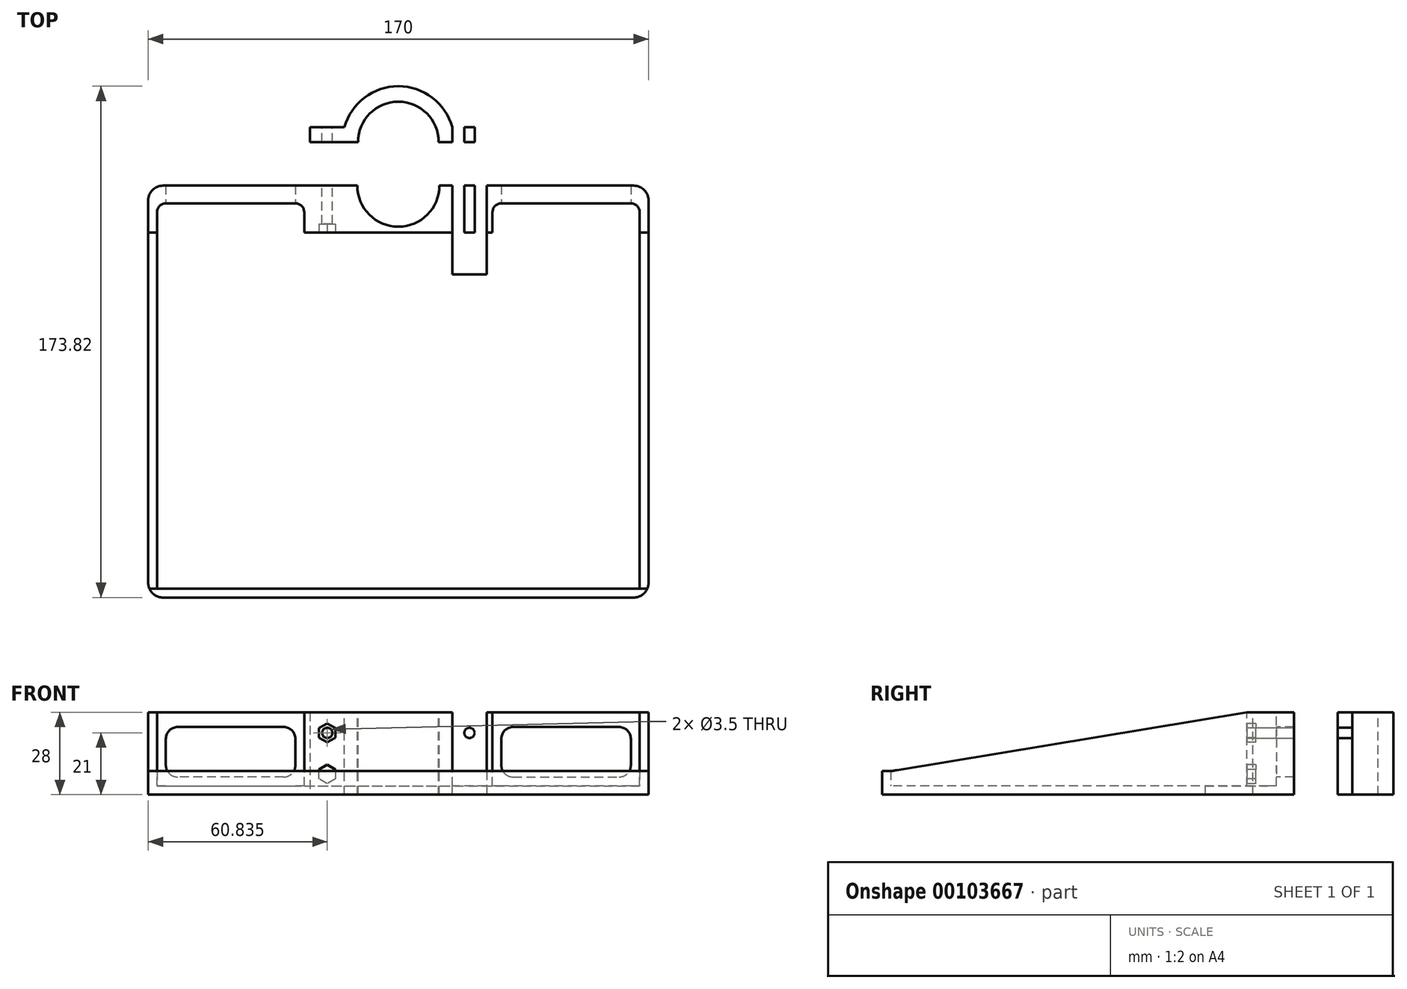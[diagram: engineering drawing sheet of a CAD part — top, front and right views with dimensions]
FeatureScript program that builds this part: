
annotation { "Feature Type Name" : "Feature", "Feature Type Description" : "" }
export const myFeature = defineFeature(function(context is Context, id is Id, definition is map)
    precondition{}
    {
        {
            var Q0;
            Q0=qCreatedBy(makeId("Top.planeOp"),FACE);
            var sketch = newSketch(context, id + "F0", { "sketchPlane" : qUnion([Q0])});
            skLineSegment(sketch, "E0.bottom", {"start": v(85, 70) * mm, "end": v(-85, 70) * mm});
            skLineSegment(sketch, "E0.top", {"start": v(85, -70) * mm, "end": v(-85, -70) * mm});
            skLineSegment(sketch, "E0.left", {"start": v(85, 70) * mm, "end": v(85, -70) * mm});
            skLineSegment(sketch, "E0.right", {"start": v(-85, 70) * mm, "end": v(-85, -70) * mm});
            skPoint(sketch, "E0.middle", {"position": v(0, 0) * mm});
            skLineSegment(sketch, "E1.bottom", {"start": v(30, 89.82) * mm, "end": v(-30, 89.82) * mm});
            skLineSegment(sketch, "E1.top", {"start": v(30, 84.82) * mm, "end": v(-30, 84.82) * mm});
            skLineSegment(sketch, "E1.left", {"start": v(30, 89.82) * mm, "end": v(30, 84.82) * mm});
            skLineSegment(sketch, "E1.right", {"start": v(-30, 89.82) * mm, "end": v(-30, 84.82) * mm});
            skPoint(sketch, "E1.middle", {"position": v(0, 87.32) * mm});
            skPoint(sketch, "E1.middle.positionSnap0", {"position": v(0, 70) * mm});
            skPoint(sketch, "E1.centerSnap0", {"position": v(0, 70) * mm});
            skSolve(sketch);
        }
        {
            var Q0;
            Q0=makeQuery(id+"F0.imprint","IMPRINT",FACE,{"disambiguationData":[TD([[makeQuery(id+"F0.imprint","IMPRINT",EDGE,{"derivedFrom":sQuery(id+"F0.wireOp",EDGE,"E0.bottom")}),1.0]])]});
            extrude(context, id + "F1", {"entities" : qUnion([Q0]), "depth" : 3 * mm});
        }
        {
            var Q0;
            Q0=makeQuery(id+"F1.opExtrude","CAP_FACE",FACE,{"disambiguationData":[OSD([sQuery(id+"F0.wireOp",EDGE,"E0.bottom"),sQuery(id+"F0.wireOp",EDGE,"E0.top"),sQuery(id+"F0.wireOp",EDGE,"E0.left"),sQuery(id+"F0.wireOp",EDGE,"E0.right")])],"isStart":false});
            var sketch = newSketch(context, id + "F2", { "sketchPlane" : qUnion([Q0])});
            skLineSegment(sketch, "E2.bottom", {"start": v(-85, 70) * mm, "end": v(85, 70) * mm});
            skLineSegment(sketch, "E2.top", {"start": v(-85, 54) * mm, "end": v(85, 54) * mm});
            skLineSegment(sketch, "E2.left", {"start": v(-85, 70) * mm, "end": v(-85, 54) * mm});
            skLineSegment(sketch, "E2.right", {"start": v(85, 70) * mm, "end": v(85, 54) * mm});
            skLineSegment(sketch, "E3.bottom", {"start": v(-85, -70) * mm, "end": v(85, -70) * mm});
            skLineSegment(sketch, "E3.top", {"start": v(-85, -67) * mm, "end": v(85, -67) * mm});
            skLineSegment(sketch, "E3.left", {"start": v(-85, -70) * mm, "end": v(-85, -67) * mm});
            skLineSegment(sketch, "E3.right", {"start": v(85, -70) * mm, "end": v(85, -67) * mm});
            skSolve(sketch);
        }
        {
            var Q0;
            Q0=makeQuery(id+"F2.imprint","IMPRINT",FACE,{"disambiguationData":[TD([[makeQuery(id+"F2.imprint","IMPRINT",EDGE,{"derivedFrom":sQuery(id+"F2.wireOp",EDGE,"E2.bottom")}),1.0]])]});
            var Q1;
            Q1=makeQuery(id+"F1.opExtrude","CAP_FACE",FACE,{"disambiguationData":[OSD([sQuery(id+"F0.wireOp",EDGE,"E1.bottom"),sQuery(id+"F0.wireOp",EDGE,"E1.top"),sQuery(id+"F0.wireOp",EDGE,"E1.left"),sQuery(id+"F0.wireOp",EDGE,"E1.right")])],"isStart":false});
            extrude(context, id + "F3", {"entities" : qUnion([Q0, Q1]), "operationType" : NewBodyOperationType.ADD, "depth" : 25 * mm});
        }
        {
            var Q0;
            Q0=makeQuery(id+"F2.imprint","IMPRINT",FACE,{"disambiguationData":[TD([[makeQuery(id+"F2.imprint","IMPRINT",EDGE,{"derivedFrom":sQuery(id+"F2.wireOp",EDGE,"E3.bottom")}),-1.0]])]});
            extrude(context, id + "F4", {"entities" : qUnion([Q0]), "operationType" : NewBodyOperationType.ADD, "depth" : 5 * mm});
        }
        {
            var Q0;
            Q0=makeQuery(id+"F3.opExtrude","CAP_FACE",FACE,{"disambiguationData":[OSD([sQuery(id+"F2.wireOp",EDGE,"E2.bottom"),sQuery(id+"F2.wireOp",EDGE,"E2.top"),sQuery(id+"F2.wireOp",EDGE,"E2.left"),sQuery(id+"F2.wireOp",EDGE,"E2.right")])],"isStart":false});
            var sketch = newSketch(context, id + "F5", { "sketchPlane" : qUnion([Q0])});
            skCircle(sketch, "E4", {"center": v(0, 70) * mm, "radius": 13.95 * mm});
            skSolve(sketch);
        }
        {
            var Q0;
            {var subQ0=sQuery(id+"F5.wireOp",EDGE,"E4");var subQ1=makeQuery(id+"F3.opExtrude","CAP_EDGE",EDGE,{"disambiguationData":[OSD([sQuery(id+"F2.wireOp",EDGE,"E2.bottom")])],"isStart":false});var subQ2=makeQuery(id+"F5.imprint","INTERSECT",VERTEX,{"disambiguationData":[OD(0.0)],"derivedFrom":[subQ1,subQ0]});Q0=makeQuery(id+"F5.imprint","IMPRINT",FACE,{"disambiguationData":[TD([[makeQuery(id+"F5.imprint","IMPRINT",EDGE,{"disambiguationData":[TD([[subQ2,-1.0]])],"derivedFrom":subQ0}),1.0]])]});}
            var Q1;
            {var subQ0=sQuery(id+"F5.wireOp",EDGE,"E4");var subQ1=makeQuery(id+"F3.opExtrude","CAP_EDGE",EDGE,{"disambiguationData":[OSD([sQuery(id+"F2.wireOp",EDGE,"E2.bottom")])],"isStart":false});var subQ2=makeQuery(id+"F5.imprint","INTERSECT",VERTEX,{"disambiguationData":[OD(0.0)],"derivedFrom":[subQ1,subQ0]});Q1=makeQuery(id+"F5.imprint","IMPRINT",FACE,{"disambiguationData":[TD([[makeQuery(id+"F5.imprint","IMPRINT",EDGE,{"disambiguationData":[TD([[subQ2,1.0]])],"derivedFrom":subQ0}),1.0]])]});}
            var Q2;
            Q2=makeQuery(id+"F1.opExtrude","CAP_FACE",FACE,{"disambiguationData":[OSD([sQuery(id+"F0.wireOp",EDGE,"E0.bottom"),sQuery(id+"F0.wireOp",EDGE,"E0.top"),sQuery(id+"F0.wireOp",EDGE,"E0.left"),sQuery(id+"F0.wireOp",EDGE,"E0.right")])],"isStart":true});
            extrude(context, id + "F6", {"entities" : qUnion([Q0, Q1]), "operationType" : NewBodyOperationType.REMOVE, "endBound" : BoundingType.UP_TO_SURFACE, "oppositeDirection" : true, "endBoundEntityFace" : qUnion([Q2]), "depth" : 25 * mm});
        }
        {
            var Q0;
            Q0=makeQuery(id+"F4.boolean.opBoolean","MERGE",FACE,{"derivedFrom":[makeQuery(id+"F3.boolean.opBoolean","MERGE",FACE,{"derivedFrom":[makeQuery(id+"F1.opExtrude","SWEPT_FACE",FACE,{"disambiguationData":[OSD([sQuery(id+"F0.wireOp",EDGE,"E0.right")])]}),makeQuery(id+"F3.opExtrude","SWEPT_FACE",FACE,{"disambiguationData":[OSD([sQuery(id+"F2.wireOp",EDGE,"E2.left")])]})]}),makeQuery(id+"F4.opExtrude","SWEPT_FACE",FACE,{"disambiguationData":[OSD([sQuery(id+"F2.wireOp",EDGE,"E3.left")])]})]});
            var sketch = newSketch(context, id + "F7", { "sketchPlane" : qUnion([Q0])});
            skLineSegment(sketch, "E5", {"start": v(-54, 28) * mm, "end": v(67, 8) * mm});
            skLineSegment(sketch, "E6", {"start": v(67, 8) * mm, "end": v(67, 3) * mm});
            skLineSegment(sketch, "E7", {"start": v(67, 3) * mm, "end": v(-54, 3) * mm});
            skLineSegment(sketch, "E8", {"start": v(-54, 3) * mm, "end": v(-54, 28) * mm});
            skSolve(sketch);
        }
        {
            var Q0;
            Q0=makeQuery(id+"F7.imprint","IMPRINT",FACE,{"disambiguationData":[TD([[makeQuery(id+"F7.imprint","IMPRINT",EDGE,{"derivedFrom":sQuery(id+"F7.wireOp",EDGE,"E5")}),-1.0]])]});
            var Q1;
            Q1 = qSketchRegion(id + "F9", true);
            extrude(context, id + "F8", {"entities" : qUnion([Q0, Q1]), "operationType" : NewBodyOperationType.ADD, "oppositeDirection" : true, "depth" : 3 * mm});
        }
        {
            var Q0;
            Q0=makeQuery(id+"F4.boolean.opBoolean","MERGE",FACE,{"derivedFrom":[makeQuery(id+"F3.boolean.opBoolean","MERGE",FACE,{"derivedFrom":[makeQuery(id+"F1.opExtrude","SWEPT_FACE",FACE,{"disambiguationData":[OSD([sQuery(id+"F0.wireOp",EDGE,"E0.left")])]}),makeQuery(id+"F3.opExtrude","SWEPT_FACE",FACE,{"disambiguationData":[OSD([sQuery(id+"F2.wireOp",EDGE,"E2.right")])]})]}),makeQuery(id+"F4.opExtrude","SWEPT_FACE",FACE,{"disambiguationData":[OSD([sQuery(id+"F2.wireOp",EDGE,"E3.right")])]})]});
            var sketch = newSketch(context, id + "F9", { "sketchPlane" : qUnion([Q0])});
            skLineSegment(sketch, "E9", {"start": v(54, 28) * mm, "end": v(-67, 8) * mm});
            skLineSegment(sketch, "E10", {"start": v(-67, 8) * mm, "end": v(-67, 3) * mm});
            skLineSegment(sketch, "E11", {"start": v(-67, 3) * mm, "end": v(54, 3) * mm});
            skLineSegment(sketch, "E12", {"start": v(54, 3) * mm, "end": v(54, 28) * mm});
            skSolve(sketch);
        }
        {
            var Q0;
            Q0=makeQuery(id+"F9.imprint","IMPRINT",FACE,{"disambiguationData":[TD([[makeQuery(id+"F9.imprint","IMPRINT",EDGE,{"derivedFrom":sQuery(id+"F9.wireOp",EDGE,"E9")}),1.0]])]});
            extrude(context, id + "F10", {"entities" : qUnion([Q0]), "operationType" : NewBodyOperationType.ADD, "oppositeDirection" : true, "depth" : 3 * mm});
        }
        {
            var Q0;
            Q0=makeQuery(id+"F0.imprint","IMPRINT",FACE,{"disambiguationData":[TD([[makeQuery(id+"F0.imprint","IMPRINT",EDGE,{"derivedFrom":sQuery(id+"F0.wireOp",EDGE,"E1.bottom")}),1.0]])]});
            extrude(context, id + "F11", {"entities" : qUnion([Q0]), "operationType" : NewBodyOperationType.ADD, "depth" : 28 * mm});
        }
        {
            var Q0;
            Q0=makeQuery(id+"F11.opExtrude","CAP_FACE",FACE,{"disambiguationData":[OSD([sQuery(id+"F0.wireOp",EDGE,"E1.bottom"),sQuery(id+"F0.wireOp",EDGE,"E1.top"),sQuery(id+"F0.wireOp",EDGE,"E1.left"),sQuery(id+"F0.wireOp",EDGE,"E1.right")])],"isStart":false});
            var sketch = newSketch(context, id + "F12", { "sketchPlane" : qUnion([Q0])});
            skArc(sketch, "E13", {"start": v(19, 84.82) * mm, "mid": v(0, 103.82) * mm, "end": v(-19, 84.82) * mm});
            skPoint(sketch, "E14", {"position": v(-19, 84.82) * mm});
            skPoint(sketch, "E15", {"position": v(19, 84.82) * mm});
            skLineSegment(sketch, "E16", {"start": v(-19, 84.82) * mm, "end": v(19, 84.82) * mm});
            skSolve(sketch);
        }
        {
            var Q0;
            {var subQ0=sQuery(id+"F12.wireOp",EDGE,"E13");var subQ1=makeQuery(id+"F11.opExtrude","CAP_EDGE",EDGE,{"disambiguationData":[OSD([sQuery(id+"F0.wireOp",EDGE,"E1.bottom")])],"isStart":false});var subQ2=makeQuery(id+"F12.imprint","INTERSECT",VERTEX,{"disambiguationData":[OD(0.0)],"derivedFrom":[subQ1,subQ0]});Q0=makeQuery(id+"F12.imprint","IMPRINT",FACE,{"disambiguationData":[TD([[makeQuery(id+"F12.imprint","IMPRINT",EDGE,{"disambiguationData":[TD([[subQ2,-1.0]])],"derivedFrom":subQ0}),1.0]])]});}
            var Q1;
            Q1=makeQuery(id+"F11.opExtrude","CAP_FACE",FACE,{"disambiguationData":[OSD([sQuery(id+"F0.wireOp",EDGE,"E1.bottom"),sQuery(id+"F0.wireOp",EDGE,"E1.top"),sQuery(id+"F0.wireOp",EDGE,"E1.left"),sQuery(id+"F0.wireOp",EDGE,"E1.right")])],"isStart":true});
            extrude(context, id + "F13", {"entities" : qUnion([Q0]), "operationType" : NewBodyOperationType.ADD, "endBound" : BoundingType.UP_TO_SURFACE, "oppositeDirection" : true, "endBoundEntityFace" : qUnion([Q1]), "depth" : 25 * mm});
        }
        {
            var Q0;
            {var subQ0=sQuery(id+"F0.wireOp",EDGE,"E1.bottom");Q0=makeQuery(id+"F13.boolean.opBoolean","MERGE",FACE,{"derivedFrom":[makeQuery(id+"F11.opExtrude","CAP_FACE",FACE,{"disambiguationData":[OSD([subQ0,sQuery(id+"F0.wireOp",EDGE,"E1.top"),sQuery(id+"F0.wireOp",EDGE,"E1.left"),sQuery(id+"F0.wireOp",EDGE,"E1.right")])],"isStart":false}),makeQuery(id+"F13.opExtrude","CAP_FACE",FACE,{"disambiguationData":[OSD([subQ0,sQuery(id+"F12.wireOp",EDGE,"E13")])],"isStart":true})]});}
            var sketch = newSketch(context, id + "F14", { "sketchPlane" : qUnion([Q0])});
            skCircle(sketch, "E17", {"center": v(0, 84.82) * mm, "radius": 13.7 * mm});
            skSolve(sketch);
        }
        {
            var Q0;
            {var subQ0=sQuery(id+"F14.wireOp",EDGE,"E17");var subQ1=makeQuery(id+"F11.opExtrude","CAP_EDGE",EDGE,{"disambiguationData":[OSD([sQuery(id+"F0.wireOp",EDGE,"E1.top")])],"isStart":false});var subQ2=makeQuery(id+"F14.imprint","INTERSECT",VERTEX,{"disambiguationData":[OD(0.0)],"derivedFrom":[subQ1,subQ0]});Q0=makeQuery(id+"F14.imprint","IMPRINT",FACE,{"disambiguationData":[TD([[makeQuery(id+"F14.imprint","IMPRINT",EDGE,{"disambiguationData":[TD([[subQ2,-1.0]])],"derivedFrom":subQ0}),1.0]])]});}
            var Q1;
            {var subQ0=sQuery(id+"F0.wireOp",EDGE,"E1.bottom");Q1=makeQuery(id+"F13.boolean.opBoolean","MERGE",FACE,{"derivedFrom":[makeQuery(id+"F11.opExtrude","CAP_FACE",FACE,{"disambiguationData":[OSD([subQ0,sQuery(id+"F0.wireOp",EDGE,"E1.top"),sQuery(id+"F0.wireOp",EDGE,"E1.left"),sQuery(id+"F0.wireOp",EDGE,"E1.right")])],"isStart":true}),makeQuery(id+"F13.opExtrude","CAP_FACE",FACE,{"disambiguationData":[OSD([subQ0,sQuery(id+"F12.wireOp",EDGE,"E13")])],"isStart":false})]});}
            extrude(context, id + "F15", {"entities" : qUnion([Q0]), "operationType" : NewBodyOperationType.REMOVE, "endBound" : BoundingType.UP_TO_SURFACE, "oppositeDirection" : true, "endBoundEntityFace" : qUnion([Q1]), "depth" : 25 * mm});
        }
        {
            var Q0;
            {var subQ1=sQuery(id+"F0.wireOp",EDGE,"E1.left");var subQ4=sQuery(id+"F0.wireOp",EDGE,"E1.bottom");Q0=makeQuery(id+"F13.boolean.opBoolean","SPLIT",FACE,{"disambiguationData":[TD([makeQuery(id+"F11.opExtrude","SWEPT_FACE",FACE,{"disambiguationData":[OSD([subQ1])]})])],"derivedFrom":makeQuery(id+"F11.opExtrude","SWEPT_FACE",FACE,{"disambiguationData":[OSD([subQ4])]})});}
            var sketch = newSketch(context, id + "F16", { "sketchPlane" : qUnion([Q0])});
            skLineSegment(sketch, "E18", {"start": v(-24.17, 28) * mm, "end": v(-24.17, 0) * mm, "construction": true});
            skCircle(sketch, "E19", {"center": v(-24.17, 7) * mm, "radius": 1.75 * mm});
            skLineSegment(sketch, "E20", {"start": v(-30, 14) * mm, "end": v(45.06, 14) * mm, "construction": true});
            skPoint(sketch, "E20.endSnap0", {"position": v(-30, 14) * mm});
            skCircle(sketch, "E21.MirrorC", {"center": v(-24.17, 21) * mm, "radius": 1.75 * mm});
            skLineSegment(sketch, "E22", {"start": v(0, 0) * mm, "end": v(0, 33.02) * mm, "construction": true});
            skCircle(sketch, "E23.MirrorC", {"center": v(24.17, 7) * mm, "radius": 1.75 * mm});
            skCircle(sketch, "E24.MirrorC", {"center": v(24.17, 21) * mm, "radius": 1.75 * mm});
            skSolve(sketch);
        }
        {
            var Q0;
            Q0=makeQuery(id+"F16.imprint","IMPRINT",FACE,{"disambiguationData":[TD([[makeQuery(id+"F16.imprint","IMPRINT",EDGE,{"derivedFrom":sQuery(id+"F16.wireOp",EDGE,"E21.MirrorC")}),-1.0]])]});
            var Q1;
            Q1=makeQuery(id+"F16.imprint","IMPRINT",FACE,{"disambiguationData":[TD([[makeQuery(id+"F16.imprint","IMPRINT",EDGE,{"derivedFrom":sQuery(id+"F16.wireOp",EDGE,"E19")}),1.0]])]});
            var Q2;
            Q2=makeQuery(id+"F16.imprint","IMPRINT",FACE,{"disambiguationData":[TD([[makeQuery(id+"F16.imprint","IMPRINT",EDGE,{"derivedFrom":sQuery(id+"F16.wireOp",EDGE,"E24.MirrorC")}),1.0]])]});
            var Q3;
            Q3=makeQuery(id+"F16.imprint","IMPRINT",FACE,{"disambiguationData":[TD([[makeQuery(id+"F16.imprint","IMPRINT",EDGE,{"derivedFrom":sQuery(id+"F16.wireOp",EDGE,"E23.MirrorC")}),-1.0]])]});
            var Q4;
            Q4=sQuery(id+"F16.wireOp",EDGE,"E21.MirrorC");
            var Q5;
            Q5=sQuery(id+"F16.wireOp",EDGE,"E19");
            var Q6;
            Q6=sQuery(id+"F16.wireOp",EDGE,"E24.MirrorC");
            var Q7;
            Q7=sQuery(id+"F16.wireOp",EDGE,"E23.MirrorC");
            extrude(context, id + "F17", {"entities" : qUnion([Q0, Q1, Q2, Q3]), "operationType" : NewBodyOperationType.REMOVE, "surfaceEntities" : qUnion([Q4, Q5, Q6, Q7]), "oppositeDirection" : true, "depth" : 50 * mm});
        }
        {
            var Q0;
            Q0=makeQuery(id+"F4.boolean.opBoolean","MERGE",EDGE,{"derivedFrom":[makeQuery(id+"F1.opExtrude","SWEPT_EDGE",EDGE,{"disambiguationData":[OSD([sQuery(id+"F0.wireOp",EDGE,"E0.top"),sQuery(id+"F0.wireOp",EDGE,"E0.left")])]}),makeQuery(id+"F4.opExtrude","SWEPT_EDGE",EDGE,{"disambiguationData":[OSD([sQuery(id+"F2.wireOp",EDGE,"E3.bottom"),sQuery(id+"F2.wireOp",EDGE,"E3.right")])]})]});
            var Q1;
            Q1=makeQuery(id+"F4.boolean.opBoolean","MERGE",EDGE,{"derivedFrom":[makeQuery(id+"F1.opExtrude","SWEPT_EDGE",EDGE,{"disambiguationData":[OSD([sQuery(id+"F0.wireOp",EDGE,"E0.top"),sQuery(id+"F0.wireOp",EDGE,"E0.right")])]}),makeQuery(id+"F4.opExtrude","SWEPT_EDGE",EDGE,{"disambiguationData":[OSD([sQuery(id+"F2.wireOp",EDGE,"E3.bottom"),sQuery(id+"F2.wireOp",EDGE,"E3.left")])]})]});
            var Q2;
            Q2=makeQuery(id+"F3.boolean.opBoolean","MERGE",EDGE,{"derivedFrom":[makeQuery(id+"F1.opExtrude","SWEPT_EDGE",EDGE,{"disambiguationData":[OSD([sQuery(id+"F0.wireOp",EDGE,"E0.bottom"),sQuery(id+"F0.wireOp",EDGE,"E0.right")])]}),makeQuery(id+"F3.opExtrude","SWEPT_EDGE",EDGE,{"disambiguationData":[OSD([sQuery(id+"F2.wireOp",EDGE,"E2.bottom"),sQuery(id+"F2.wireOp",EDGE,"E2.left")])]})]});
            var Q3;
            Q3=makeQuery(id+"F3.boolean.opBoolean","MERGE",EDGE,{"derivedFrom":[makeQuery(id+"F1.opExtrude","SWEPT_EDGE",EDGE,{"disambiguationData":[OSD([sQuery(id+"F0.wireOp",EDGE,"E0.bottom"),sQuery(id+"F0.wireOp",EDGE,"E0.left")])]}),makeQuery(id+"F3.opExtrude","SWEPT_EDGE",EDGE,{"disambiguationData":[OSD([sQuery(id+"F2.wireOp",EDGE,"E2.bottom"),sQuery(id+"F2.wireOp",EDGE,"E2.right")])]})]});
            fillet(context, id + "F18", {"entities" : qUnion([Q0, Q1, Q2, Q3]), "radius" : 5 * mm, "tangentPropagation" : true, "allowEdgeOverflow" : false});
        }
        {
            var Q0;
            Q0=makeQuery(id+"F3.opExtrude","CAP_FACE",FACE,{"disambiguationData":[OSD([sQuery(id+"F2.wireOp",EDGE,"E2.bottom"),sQuery(id+"F2.wireOp",EDGE,"E2.top"),sQuery(id+"F2.wireOp",EDGE,"E2.left"),sQuery(id+"F2.wireOp",EDGE,"E2.right")])],"isStart":false});
            var sketch = newSketch(context, id + "F19", { "sketchPlane" : qUnion([Q0])});
            skLineSegment(sketch, "E25.bottom", {"start": v(-82, 54) * mm, "end": v(-32, 54) * mm});
            skLineSegment(sketch, "E25.top", {"start": v(-82, 64) * mm, "end": v(-32, 64) * mm});
            skLineSegment(sketch, "E25.left", {"start": v(-82, 54) * mm, "end": v(-82, 64) * mm});
            skLineSegment(sketch, "E25.right", {"start": v(-32, 54) * mm, "end": v(-32, 64) * mm});
            skPoint(sketch, "E26.endSnap0", {"position": v(0, 56.05) * mm});
            skLineSegment(sketch, "E27", {"start": v(0, 54) * mm, "end": v(0, 56.05) * mm});
            skLineSegment(sketch, "E28.MirrorCS", {"start": v(-82, 64) * mm, "end": v(-132, 64) * mm});
            skLineSegment(sketch, "E29.MirrorCS", {"start": v(-132, 54) * mm, "end": v(-132, 64) * mm});
            skLineSegment(sketch, "E30.MirrorCS", {"start": v(-82, 54) * mm, "end": v(-132, 54) * mm});
            skLineSegment(sketch, "E31.MirrorCS", {"start": v(82, 54) * mm, "end": v(82, 64) * mm});
            skLineSegment(sketch, "E32.MirrorCS", {"start": v(82, 54) * mm, "end": v(32, 54) * mm});
            skLineSegment(sketch, "E33.MirrorCS", {"start": v(32, 54) * mm, "end": v(32, 64) * mm});
            skLineSegment(sketch, "E34.MirrorCS", {"start": v(82, 64) * mm, "end": v(32, 64) * mm});
            skSolve(sketch);
        }
        {
            var Q0;
            Q0=makeQuery(id+"F19.imprint","IMPRINT",FACE,{"disambiguationData":[TD([[makeQuery(id+"F19.imprint","IMPRINT",EDGE,{"derivedFrom":sQuery(id+"F19.wireOp",EDGE,"E25.bottom")}),1.0]])]});
            var Q1;
            Q1=makeQuery(id+"F19.imprint","IMPRINT",FACE,{"disambiguationData":[TD([[makeQuery(id+"F19.imprint","IMPRINT",EDGE,{"derivedFrom":sQuery(id+"F19.wireOp",EDGE,"E31.MirrorCS")}),1.0]])]});
            extrude(context, id + "F20", {"entities" : qUnion([Q0, Q1]), "operationType" : NewBodyOperationType.REMOVE, "oppositeDirection" : true, "depth" : 25 * mm});
        }
        {
            var Q0;
            Q0=makeQuery(id+"F20.boolean.opBoolean","COPY",EDGE,{"derivedFrom":makeQuery(id+"F20.opExtrude","SWEPT_EDGE",EDGE,{"disambiguationData":[OSD([sQuery(id+"F2.wireOp",EDGE,"E2.top"),sQuery(id+"F19.wireOp",EDGE,"E25.bottom"),sQuery(id+"F19.wireOp",EDGE,"E25.right")])]})});
            var Q1;
            Q1=makeQuery(id+"F20.boolean.opBoolean","COPY",EDGE,{"derivedFrom":makeQuery(id+"F20.opExtrude","SWEPT_EDGE",EDGE,{"disambiguationData":[OSD([sQuery(id+"F2.wireOp",EDGE,"E2.top"),sQuery(id+"F19.wireOp",EDGE,"E32.MirrorCS"),sQuery(id+"F19.wireOp",EDGE,"E33.MirrorCS")])]})});
            var Q2;
            Q2=makeQuery(id+"F20.boolean.opBoolean","COPY",EDGE,{"derivedFrom":makeQuery(id+"F20.opExtrude","SWEPT_EDGE",EDGE,{"disambiguationData":[OSD([sQuery(id+"F19.wireOp",EDGE,"E25.top"),sQuery(id+"F19.wireOp",EDGE,"E25.left"),sQuery(id+"F19.wireOp",EDGE,"E28.MirrorCS")])]})});
            var Q3;
            Q3=makeQuery(id+"F20.boolean.opBoolean","COPY",EDGE,{"derivedFrom":makeQuery(id+"F20.opExtrude","SWEPT_EDGE",EDGE,{"disambiguationData":[OSD([sQuery(id+"F19.wireOp",EDGE,"E25.top"),sQuery(id+"F19.wireOp",EDGE,"E25.right")])]})});
            var Q4;
            Q4=makeQuery(id+"F20.boolean.opBoolean","COPY",EDGE,{"derivedFrom":makeQuery(id+"F20.opExtrude","SWEPT_EDGE",EDGE,{"disambiguationData":[OSD([sQuery(id+"F19.wireOp",EDGE,"E31.MirrorCS"),sQuery(id+"F19.wireOp",EDGE,"E34.MirrorCS")])]})});
            var Q5;
            Q5=makeQuery(id+"F20.boolean.opBoolean","COPY",EDGE,{"derivedFrom":makeQuery(id+"F20.opExtrude","SWEPT_EDGE",EDGE,{"disambiguationData":[OSD([sQuery(id+"F19.wireOp",EDGE,"E33.MirrorCS"),sQuery(id+"F19.wireOp",EDGE,"E34.MirrorCS")])]})});
            var Q6;
            Q6=makeQuery(id+"F10.opExtrude","CAP_EDGE",EDGE,{"disambiguationData":[OSD([sQuery(id+"F9.wireOp",EDGE,"E10")])],"isStart":false});
            var Q7;
            Q7=makeQuery(id+"F8.opExtrude","CAP_EDGE",EDGE,{"disambiguationData":[OSD([sQuery(id+"F7.wireOp",EDGE,"E6")])],"isStart":false});
            fillet(context, id + "F21", {"entities" : qUnion([Q0, Q1, Q2, Q3, Q4, Q5, Q6, Q7]), "radius" : 3 * mm, "tangentPropagation" : true, "allowEdgeOverflow" : false});
        }
        {
            var Q0;
            Q0=makeQuery(id+"F20.boolean.opBoolean","COPY",FACE,{"derivedFrom":makeQuery(id+"F20.opExtrude","SWEPT_FACE",FACE,{"disambiguationData":[OSD([sQuery(id+"F19.wireOp",EDGE,"E25.top")])]})});
            var sketch = newSketch(context, id + "F22", { "sketchPlane" : qUnion([Q0])});
            skLineSegment(sketch, "E35.bottom", {"start": v(-79, 23) * mm, "end": v(-35, 23) * mm});
            skLineSegment(sketch, "E35.top", {"start": v(-79, 6) * mm, "end": v(-35, 6) * mm});
            skLineSegment(sketch, "E35.left", {"start": v(-79, 23) * mm, "end": v(-79, 6) * mm});
            skLineSegment(sketch, "E35.right", {"start": v(-35, 23) * mm, "end": v(-35, 6) * mm});
            skLineSegment(sketch, "E36", {"start": v(0, 0) * mm, "end": v(0, 35.25) * mm, "construction": true});
            skLineSegment(sketch, "E37.MirrorCS", {"start": v(79, 23) * mm, "end": v(35, 23) * mm});
            skLineSegment(sketch, "E38.MirrorCS", {"start": v(79, 23) * mm, "end": v(79, 6) * mm});
            skLineSegment(sketch, "E39.MirrorCS", {"start": v(79, 6) * mm, "end": v(35, 6) * mm});
            skLineSegment(sketch, "E40.MirrorCS", {"start": v(35, 23) * mm, "end": v(35, 6) * mm});
            skSolve(sketch);
        }
        {
            var Q0;
            Q0=makeQuery(id+"F22.imprint","IMPRINT",FACE,{"disambiguationData":[TD([[makeQuery(id+"F22.imprint","IMPRINT",EDGE,{"derivedFrom":sQuery(id+"F22.wireOp",EDGE,"E35.bottom")}),-1.0]])]});
            var Q1;
            Q1=makeQuery(id+"F22.imprint","IMPRINT",FACE,{"disambiguationData":[TD([[makeQuery(id+"F22.imprint","IMPRINT",EDGE,{"derivedFrom":sQuery(id+"F22.wireOp",EDGE,"E37.MirrorCS")}),1.0]])]});
            var Q2;
            {var subQ1=sQuery(id+"F2.wireOp",EDGE,"E2.bottom");var subQ2=sQuery(id+"F0.wireOp",EDGE,"E0.left");var subQ3=sQuery(id+"F0.wireOp",EDGE,"E0.bottom");Q2=makeQuery(id+"F6.boolean.opBoolean","SPLIT",FACE,{"disambiguationData":[TD([makeQuery(id+"F1.opExtrude","SWEPT_FACE",FACE,{"disambiguationData":[OSD([subQ2])]})])],"derivedFrom":makeQuery(id+"F3.boolean.opBoolean","MERGE",FACE,{"derivedFrom":[makeQuery(id+"F1.opExtrude","SWEPT_FACE",FACE,{"disambiguationData":[OSD([subQ3])]}),makeQuery(id+"F3.opExtrude","SWEPT_FACE",FACE,{"disambiguationData":[OSD([subQ1])]})]})});}
            extrude(context, id + "F23", {"entities" : qUnion([Q0, Q1]), "operationType" : NewBodyOperationType.REMOVE, "endBound" : BoundingType.UP_TO_SURFACE, "oppositeDirection" : true, "endBoundEntityFace" : qUnion([Q2]), "depth" : 25 * mm});
        }
        {
            var Q0;
            Q0=makeQuery(id+"F23.boolean.opBoolean","COPY",EDGE,{"derivedFrom":makeQuery(id+"F23.opExtrude","SWEPT_EDGE",EDGE,{"disambiguationData":[OSD([sQuery(id+"F19.wireOp",EDGE,"E25.top"),sQuery(id+"F19.wireOp",EDGE,"E25.left"),sQuery(id+"F19.wireOp",EDGE,"E28.MirrorCS"),sQuery(id+"F22.wireOp",EDGE,"E35.top"),sQuery(id+"F22.wireOp",EDGE,"E35.left")])]})});
            var Q1;
            Q1=makeQuery(id+"F23.boolean.opBoolean","COPY",EDGE,{"derivedFrom":makeQuery(id+"F23.opExtrude","SWEPT_EDGE",EDGE,{"disambiguationData":[OSD([sQuery(id+"F19.wireOp",EDGE,"E25.top"),sQuery(id+"F19.wireOp",EDGE,"E25.right"),sQuery(id+"F22.wireOp",EDGE,"E35.top"),sQuery(id+"F22.wireOp",EDGE,"E35.right")])]})});
            var Q2;
            Q2=makeQuery(id+"F23.boolean.opBoolean","COPY",EDGE,{"derivedFrom":makeQuery(id+"F23.opExtrude","SWEPT_EDGE",EDGE,{"disambiguationData":[OSD([sQuery(id+"F19.wireOp",EDGE,"E25.top"),sQuery(id+"F19.wireOp",EDGE,"E25.right"),sQuery(id+"F22.wireOp",EDGE,"E35.bottom"),sQuery(id+"F22.wireOp",EDGE,"E35.right")])]})});
            var Q3;
            Q3=makeQuery(id+"F23.boolean.opBoolean","COPY",EDGE,{"derivedFrom":makeQuery(id+"F23.opExtrude","SWEPT_EDGE",EDGE,{"disambiguationData":[OSD([sQuery(id+"F19.wireOp",EDGE,"E25.top"),sQuery(id+"F19.wireOp",EDGE,"E25.left"),sQuery(id+"F19.wireOp",EDGE,"E28.MirrorCS"),sQuery(id+"F22.wireOp",EDGE,"E35.bottom"),sQuery(id+"F22.wireOp",EDGE,"E35.left")])]})});
            var Q4;
            Q4=makeQuery(id+"F23.boolean.opBoolean","COPY",EDGE,{"derivedFrom":makeQuery(id+"F23.opExtrude","SWEPT_EDGE",EDGE,{"disambiguationData":[OSD([sQuery(id+"F22.wireOp",EDGE,"E39.MirrorCS"),sQuery(id+"F22.wireOp",EDGE,"E40.MirrorCS")])]})});
            var Q5;
            Q5=makeQuery(id+"F23.boolean.opBoolean","COPY",EDGE,{"derivedFrom":makeQuery(id+"F23.opExtrude","SWEPT_EDGE",EDGE,{"disambiguationData":[OSD([sQuery(id+"F22.wireOp",EDGE,"E37.MirrorCS"),sQuery(id+"F22.wireOp",EDGE,"E40.MirrorCS")])]})});
            var Q6;
            Q6=makeQuery(id+"F23.boolean.opBoolean","COPY",EDGE,{"derivedFrom":makeQuery(id+"F23.opExtrude","SWEPT_EDGE",EDGE,{"disambiguationData":[OSD([sQuery(id+"F22.wireOp",EDGE,"E37.MirrorCS"),sQuery(id+"F22.wireOp",EDGE,"E38.MirrorCS")])]})});
            var Q7;
            Q7=makeQuery(id+"F23.boolean.opBoolean","COPY",EDGE,{"derivedFrom":makeQuery(id+"F23.opExtrude","SWEPT_EDGE",EDGE,{"disambiguationData":[OSD([sQuery(id+"F22.wireOp",EDGE,"E38.MirrorCS"),sQuery(id+"F22.wireOp",EDGE,"E39.MirrorCS")])]})});
            fillet(context, id + "F24", {"entities" : qUnion([Q0, Q1, Q2, Q3, Q4, Q5, Q6, Q7]), "radius" : 4 * mm, "tangentPropagation" : true, "allowEdgeOverflow" : false});
        }
        {
            var Q0;
            Q0=makeQuery(id+"F3.opExtrude","SWEPT_FACE",FACE,{"disambiguationData":[OSD([sQuery(id+"F2.wireOp",EDGE,"E2.top")])]});
            var sketch = newSketch(context, id + "F25", { "sketchPlane" : qUnion([Q0])});
            skCircle(sketch, "E41.cCircle", {"center": v(-24.17, 21) * mm, "radius": 2.8 * mm, "construction": true});
            skLineSegment(sketch, "E41.0", {"start": v(-24.17, 24.23) * mm, "end": v(-21.37, 22.62) * mm});
            skLineSegment(sketch, "E41.1", {"start": v(-21.37, 22.62) * mm, "end": v(-21.37, 19.38) * mm});
            skLineSegment(sketch, "E41.2", {"start": v(-21.37, 19.38) * mm, "end": v(-24.17, 17.77) * mm});
            skLineSegment(sketch, "E41.3", {"start": v(-24.17, 17.77) * mm, "end": v(-26.97, 19.38) * mm});
            skLineSegment(sketch, "E41.4", {"start": v(-26.97, 19.38) * mm, "end": v(-26.97, 22.62) * mm});
            skLineSegment(sketch, "E41.5", {"start": v(-26.97, 22.62) * mm, "end": v(-24.17, 24.23) * mm});
            skPoint(sketch, "E41.0.midPoint", {"position": v(-22.77, 23.42) * mm});
            skCircle(sketch, "E42.cCircle", {"center": v(-24.17, 7) * mm, "radius": 2.8 * mm, "construction": true});
            skLineSegment(sketch, "E42.0", {"start": v(-24.17, 10.23) * mm, "end": v(-21.37, 8.62) * mm});
            skLineSegment(sketch, "E42.1", {"start": v(-21.37, 8.62) * mm, "end": v(-21.37, 5.38) * mm});
            skLineSegment(sketch, "E42.2", {"start": v(-21.37, 5.38) * mm, "end": v(-24.17, 3.77) * mm});
            skLineSegment(sketch, "E42.3", {"start": v(-24.17, 3.77) * mm, "end": v(-26.97, 5.38) * mm});
            skLineSegment(sketch, "E42.4", {"start": v(-26.97, 5.38) * mm, "end": v(-26.97, 8.62) * mm});
            skLineSegment(sketch, "E42.5", {"start": v(-26.97, 8.62) * mm, "end": v(-24.17, 10.23) * mm});
            skPoint(sketch, "E42.0.midPoint", {"position": v(-22.77, 9.42) * mm});
            skCircle(sketch, "E43.cCircle", {"center": v(24.17, 21) * mm, "radius": 2.8 * mm, "construction": true});
            skLineSegment(sketch, "E43.0", {"start": v(24.17, 24.23) * mm, "end": v(26.97, 22.62) * mm});
            skLineSegment(sketch, "E43.1", {"start": v(26.97, 22.62) * mm, "end": v(26.97, 19.38) * mm});
            skLineSegment(sketch, "E43.2", {"start": v(26.97, 19.38) * mm, "end": v(24.17, 17.77) * mm});
            skLineSegment(sketch, "E43.3", {"start": v(24.17, 17.77) * mm, "end": v(21.37, 19.38) * mm});
            skLineSegment(sketch, "E43.4", {"start": v(21.37, 19.38) * mm, "end": v(21.37, 22.62) * mm});
            skLineSegment(sketch, "E43.5", {"start": v(21.37, 22.62) * mm, "end": v(24.17, 24.23) * mm});
            skPoint(sketch, "E43.0.midPoint", {"position": v(25.57, 23.42) * mm});
            skCircle(sketch, "E44.cCircle", {"center": v(24.17, 7) * mm, "radius": 2.8 * mm, "construction": true});
            skLineSegment(sketch, "E44.0", {"start": v(24.17, 10.23) * mm, "end": v(26.97, 8.62) * mm});
            skLineSegment(sketch, "E44.1", {"start": v(26.97, 8.62) * mm, "end": v(26.97, 5.38) * mm});
            skLineSegment(sketch, "E44.2", {"start": v(26.97, 5.38) * mm, "end": v(24.17, 3.77) * mm});
            skLineSegment(sketch, "E44.3", {"start": v(24.17, 3.77) * mm, "end": v(21.37, 5.38) * mm});
            skLineSegment(sketch, "E44.4", {"start": v(21.37, 5.38) * mm, "end": v(21.37, 8.62) * mm});
            skLineSegment(sketch, "E44.5", {"start": v(21.37, 8.62) * mm, "end": v(24.17, 10.23) * mm});
            skPoint(sketch, "E44.0.midPoint", {"position": v(25.57, 9.42) * mm});
            skSolve(sketch);
        }
        {
            var Q0;
            Q0=makeQuery(id+"F25.imprint","IMPRINT",FACE,{"disambiguationData":[TD([[makeQuery(id+"F25.imprint","IMPRINT",EDGE,{"derivedFrom":sQuery(id+"F25.wireOp",EDGE,"E41.0")}),-1.0]])]});
            var Q1;
            Q1=makeQuery(id+"F25.imprint","IMPRINT",FACE,{"disambiguationData":[TD([[makeQuery(id+"F25.imprint","IMPRINT",EDGE,{"derivedFrom":sQuery(id+"F25.wireOp",EDGE,"E42.0")}),-1.0]])]});
            var Q2;
            Q2=makeQuery(id+"F25.imprint","IMPRINT",FACE,{"disambiguationData":[TD([[makeQuery(id+"F25.imprint","IMPRINT",EDGE,{"derivedFrom":sQuery(id+"F25.wireOp",EDGE,"E43.0")}),-1.0]])]});
            var Q3;
            Q3=makeQuery(id+"F25.imprint","IMPRINT",FACE,{"disambiguationData":[TD([[makeQuery(id+"F25.imprint","IMPRINT",EDGE,{"derivedFrom":sQuery(id+"F25.wireOp",EDGE,"E44.0")}),-1.0]])]});
            extrude(context, id + "F26", {"entities" : qUnion([Q0, Q1, Q2, Q3]), "operationType" : NewBodyOperationType.REMOVE, "oppositeDirection" : true, "depth" : 3 * mm});
        }
    });
